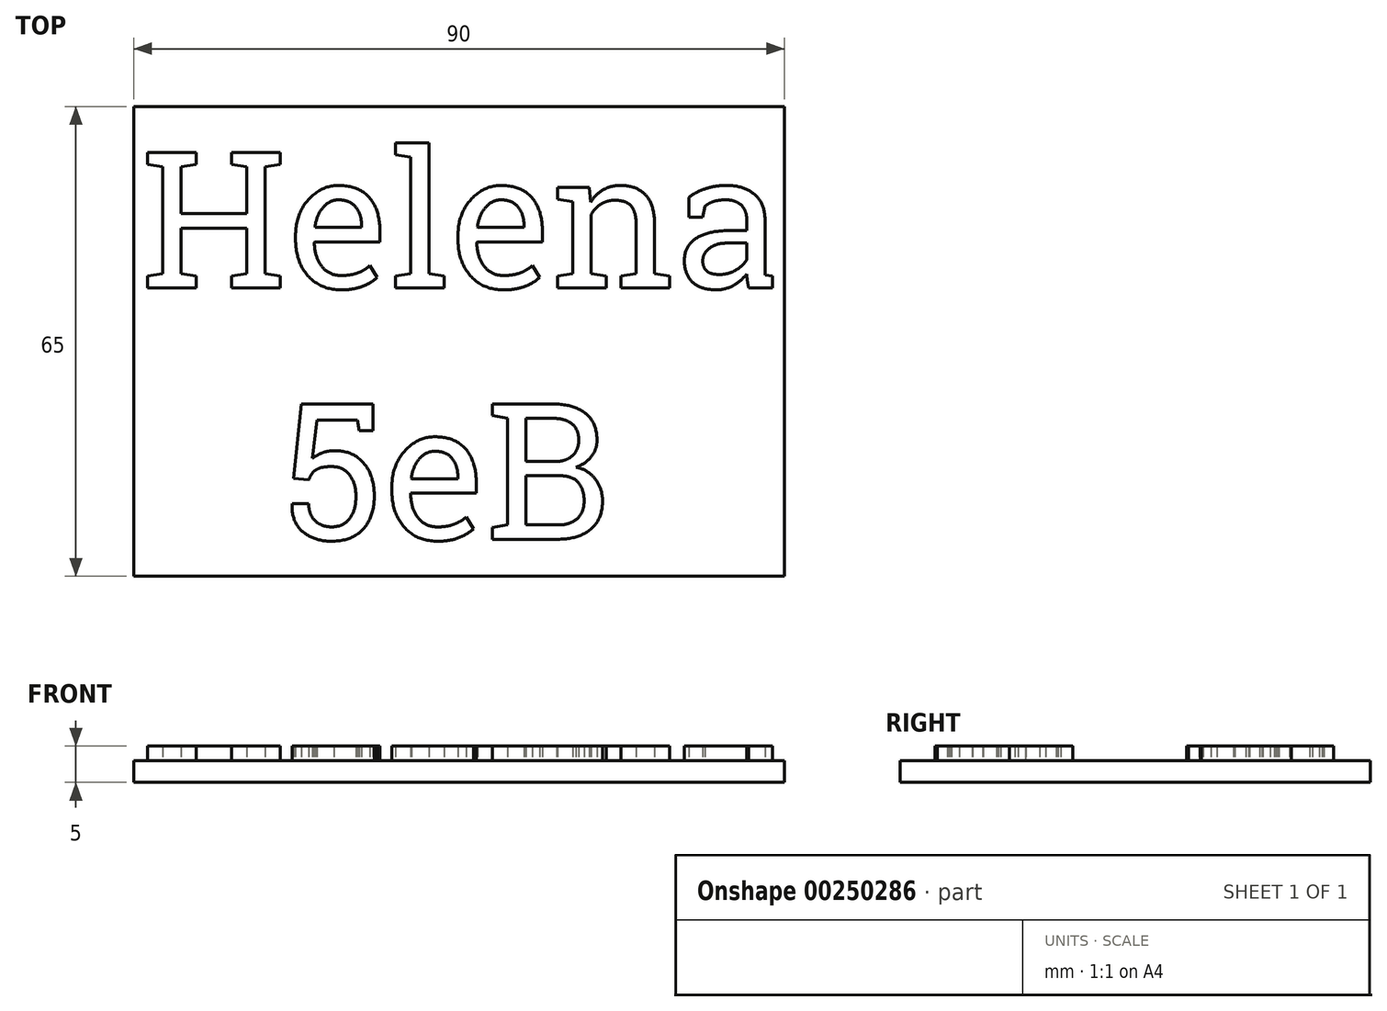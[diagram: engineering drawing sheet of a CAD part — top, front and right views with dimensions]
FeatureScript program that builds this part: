
annotation { "Feature Type Name" : "Feature", "Feature Type Description" : "" }
export const myFeature = defineFeature(function(context is Context, id is Id, definition is map)
    precondition{}
    {
        {
            var Q0;
            Q0=qCreatedBy(makeId("Top.planeOp"),FACE);
            var sketch = newSketch(context, id + "F0", { "sketchPlane" : qUnion([Q0])});
            skLineSegment(sketch, "E0.bottom", {"start": v(0, 0) * mm, "end": v(90, 0) * mm});
            skLineSegment(sketch, "E0.top", {"start": v(0, -65) * mm, "end": v(90, -65) * mm});
            skLineSegment(sketch, "E0.left", {"start": v(0, 0) * mm, "end": v(0, -65) * mm});
            skLineSegment(sketch, "E0.right", {"start": v(90, 0) * mm, "end": v(90, -65) * mm});
            skSolve(sketch);
        }
        {
            var Q0;
            Q0=makeQuery(id+"F0.imprint","IMPRINT",FACE,{"disambiguationData":[TD([[makeQuery(id+"F0.imprint","IMPRINT",EDGE,{"derivedFrom":sQuery(id+"F0.wireOp",EDGE,"E0.bottom")}),-1.0]])]});
            extrude(context, id + "F1", {"entities" : qUnion([Q0]), "depth" : 3 * mm});
        }
        {
            var Q0;
            Q0=makeQuery(id+"F1.opExtrude","CAP_FACE",FACE,{"disambiguationData":[OSD([sQuery(id+"F0.wireOp",EDGE,"E0.bottom"),sQuery(id+"F0.wireOp",EDGE,"E0.top"),sQuery(id+"F0.wireOp",EDGE,"E0.left"),sQuery(id+"F0.wireOp",EDGE,"E0.right")])],"isStart":false});
            var sketch = newSketch(context, id + "F2", { "sketchPlane" : qUnion([Q0])});
            skText(sketch, "E1", { "text": "Helena\n   5eB", "fontName": "RobotoSlab-Regular.ttf"});
            const initialGuessF2  = {"E1": [0.001, -0.0251, 1, 0, 0.01897]};
            skSetInitialGuess(sketch, initialGuessF2);
            skSolve(sketch);
        }
        {
            var Q0;
            Q0 = qSketchRegion(id + "F2", true);
            extrude(context, id + "F3", {"entities" : qUnion([Q0]), "operationType" : NewBodyOperationType.ADD, "depth" : 2 * mm});
        }
    });
